# Revit family: ALMA-Cam_Cavity_Sliding_Door_Lock
name_source: partatom
category: Specialty Equipment
units: mm (PartAtom-declared; Revit-internal decimal feet)

## family parameters
Always vertical = Yes
Cut with Voids When Loaded = No
Enable Cutting in Views = Yes
Maintain Annotation Orientation = No
Part Type = Normal
Room Calculation Point = No
Round Connector Dimension = Use Diameter
Shared = No
Work Plane-Based = Yes

## types (5) — shared parameters
Deadbolt_Material = BM_STAINLESS STEEL_POLISHED
Default Elevation = 1219 mm
Door Lock Depth = 12 mm  [stored 0.0393701 ft]
Door Lock Width = 62 mm
Faceplate Height = 104 mm
Faceplate Width = 20 mm  [stored 0.0656168 ft]
InWallBody_Material = BM_MATTE BLACK
Spindle_Material = BM_STAINLESS STEEL_POLISHED

## per-type parameters (varying)
| type | DoorLock_Material |
| MATTE BLACK (DHSLMB01) | BM_MATTE BLACK |
| BRUSHED BRASS GOLD (DHSLGD02) | BM_BRASS GOLD |
| BRUSHED ANTIQUE BRASS (DHSLVB05) | BM_ANTIQUE BRASS |
| BRUSHED NICKEL (DHSLBN04) | BM_NICKEL |
| BRUSHED GUNMETAL (DHSLGM03) | BM_GUNMETAL |

note: [stored X ft] marks values corroborated as IEEE doubles in the binary element streams (Revit-internal decimal feet)

## geometry (parser evidence)
native form markers: Sweep x1
no freeform markers — native parametric forms only
